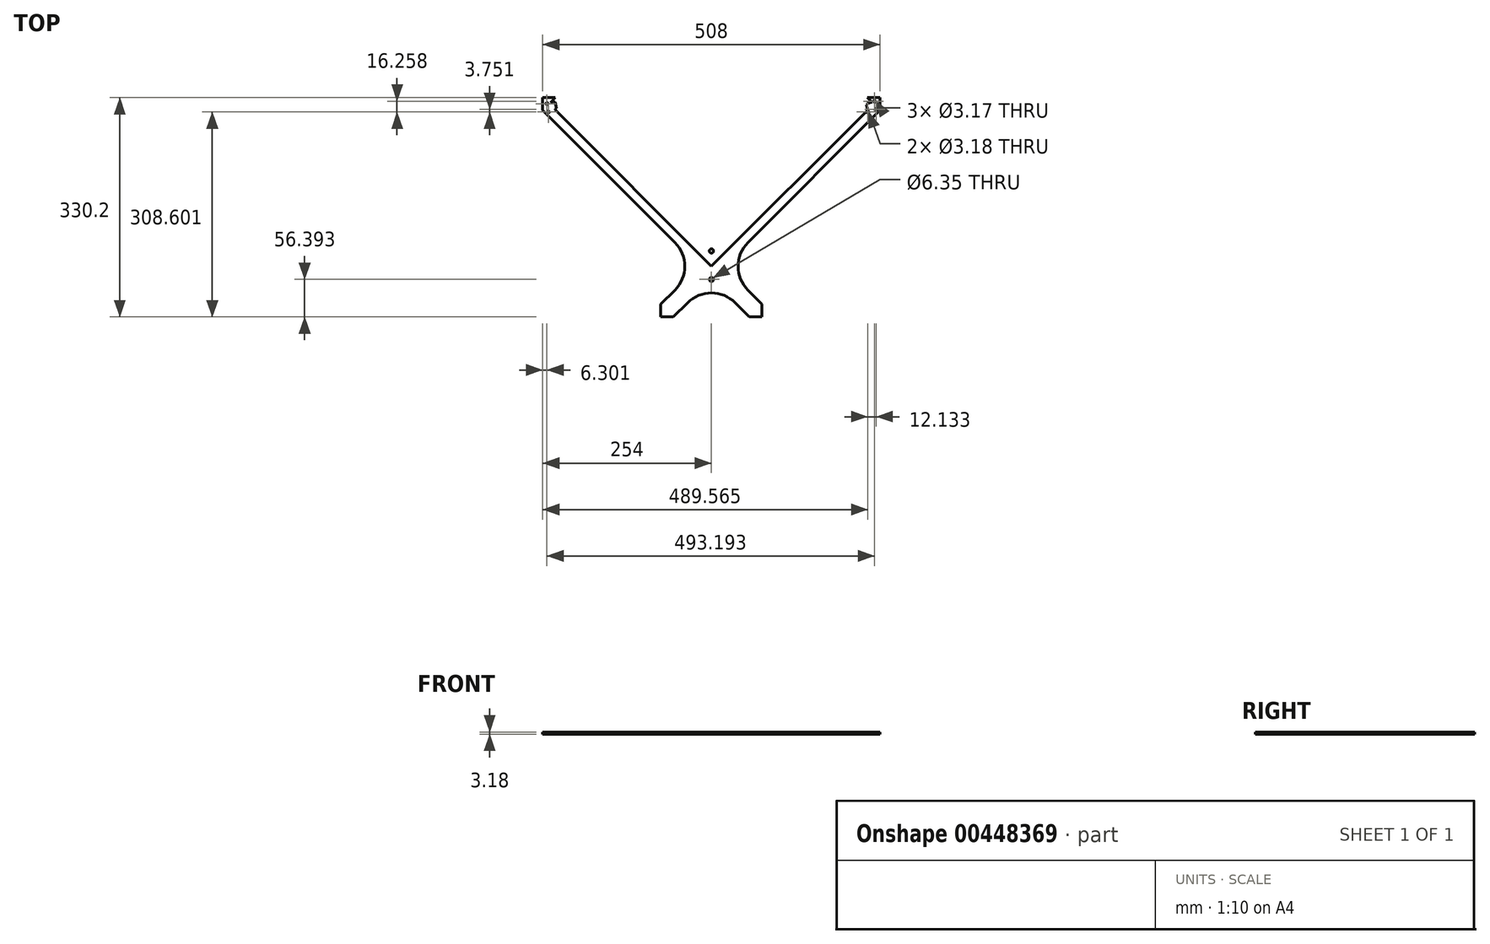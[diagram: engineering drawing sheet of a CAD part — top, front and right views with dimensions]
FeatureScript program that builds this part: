
annotation { "Feature Type Name" : "Feature", "Feature Type Description" : "" }
export const myFeature = defineFeature(function(context is Context, id is Id, definition is map)
    precondition{}
    {
        {
            var Q0;
            Q0=qCreatedBy(makeId("Top.planeOp"),FACE);
            var sketch = newSketch(context, id + "F0", { "sketchPlane" : qUnion([Q0])});
            skLineSegment(sketch, "E0.bottom", {"start": v(254, 254) * mm, "end": v(-254, 254) * mm});
            skLineSegment(sketch, "E0.top", {"start": v(254, -254) * mm, "end": v(-254, -254) * mm});
            skLineSegment(sketch, "E0.left", {"start": v(254, 254) * mm, "end": v(254, -254) * mm});
            skLineSegment(sketch, "E0.right", {"start": v(-254, 254) * mm, "end": v(-254, -254) * mm});
            skPoint(sketch, "E0.middle", {"position": v(0, 0) * mm});
            skSolve(sketch);
        }
        {
            var Q0;
            Q0=makeQuery(id+"F0.imprint","IMPRINT",FACE,{"disambiguationData":[TD([[makeQuery(id+"F0.imprint","IMPRINT",EDGE,{"derivedFrom":sQuery(id+"F0.wireOp",EDGE,"E0.bottom")}),1.0]])]});
            extrude(context, id + "F1", {"entities" : qUnion([Q0]), "depth" : 3.17 * mm});
        }
        {
            var Q0;
            Q0=makeQuery(id+"F1.opExtrude","CAP_FACE",FACE,{"disambiguationData":[OSD([sQuery(id+"F0.wireOp",EDGE,"E0.bottom"),sQuery(id+"F0.wireOp",EDGE,"E0.top"),sQuery(id+"F0.wireOp",EDGE,"E0.left"),sQuery(id+"F0.wireOp",EDGE,"E0.right")])],"isStart":false});
            var sketch = newSketch(context, id + "F2", { "sketchPlane" : qUnion([Q0])});
            skLineSegment(sketch, "E1", {"start": v(0, 19.05) * mm, "end": v(234.95, 254) * mm});
            skLineSegment(sketch, "E2", {"start": v(19.05, 0) * mm, "end": v(254, 234.95) * mm});
            skLineSegment(sketch, "E3.MirrorCS", {"start": v(0, 19.05) * mm, "end": v(-234.95, 254) * mm});
            skLineSegment(sketch, "E4.MirrorCS", {"start": v(-19.05, 0) * mm, "end": v(-254, 234.95) * mm});
            skLineSegment(sketch, "E5.MirrorCS", {"start": v(19.05, 0) * mm, "end": v(254, -234.95) * mm});
            skLineSegment(sketch, "E6.MirrorCS", {"start": v(-19.05, 0) * mm, "end": v(-254, -234.95) * mm});
            skLineSegment(sketch, "E7.MirrorCS", {"start": v(0, -19.05) * mm, "end": v(-234.95, -254) * mm});
            skLineSegment(sketch, "E8.MirrorCS", {"start": v(0, -19.05) * mm, "end": v(234.95, -254) * mm});
            skLineSegment(sketch, "E9", {"start": v(-234.95, 254) * mm, "end": v(234.95, 254) * mm});
            skLineSegment(sketch, "E10", {"start": v(254, 234.95) * mm, "end": v(254, -234.95) * mm});
            skLineSegment(sketch, "E11", {"start": v(-254, -234.95) * mm, "end": v(-254, 234.95) * mm});
            skLineSegment(sketch, "E12", {"start": v(-234.95, -254) * mm, "end": v(234.95, -254) * mm});
            skLineSegment(sketch, "E13", {"start": v(0, 0) * mm, "end": v(254, -254) * mm});
            skSolve(sketch);
        }
        {
            var Q0;
            Q0=makeQuery(id+"F2.imprint","IMPRINT",FACE,{"disambiguationData":[TD([[makeQuery(id+"F2.imprint","IMPRINT",EDGE,{"derivedFrom":sQuery(id+"F2.wireOp",EDGE,"E4.MirrorCS")}),1.0]])]});
            var Q1;
            Q1=makeQuery(id+"F2.imprint","IMPRINT",FACE,{"disambiguationData":[TD([[makeQuery(id+"F2.imprint","IMPRINT",EDGE,{"derivedFrom":sQuery(id+"F2.wireOp",EDGE,"E1")}),1.0]])]});
            var Q2;
            Q2=makeQuery(id+"F2.imprint","IMPRINT",FACE,{"disambiguationData":[TD([[makeQuery(id+"F2.imprint","IMPRINT",EDGE,{"derivedFrom":sQuery(id+"F2.wireOp",EDGE,"E2")}),-1.0]])]});
            var Q3;
            Q3=makeQuery(id+"F2.imprint","IMPRINT",FACE,{"disambiguationData":[TD([[makeQuery(id+"F2.imprint","IMPRINT",EDGE,{"derivedFrom":sQuery(id+"F2.wireOp",EDGE,"E7.MirrorCS")}),1.0]])]});
            extrude(context, id + "F3", {"entities" : qUnion([Q0, Q1, Q2, Q3]), "operationType" : NewBodyOperationType.REMOVE, "endBound" : BoundingType.THROUGH_ALL, "oppositeDirection" : true, "depth" : 25.4 * mm});
        }
        {
            var Q0;
            Q0=makeQuery(id+"F3.boolean.opBoolean","COPY",EDGE,{"derivedFrom":makeQuery(id+"F3.opExtrude","SWEPT_EDGE",EDGE,{"disambiguationData":[OSD([sQuery(id+"F2.wireOp",EDGE,"E4.MirrorCS"),sQuery(id+"F2.wireOp",EDGE,"E6.MirrorCS")])]})});
            var Q1;
            Q1=makeQuery(id+"F3.boolean.opBoolean","COPY",EDGE,{"derivedFrom":makeQuery(id+"F3.opExtrude","SWEPT_EDGE",EDGE,{"disambiguationData":[OSD([sQuery(id+"F2.wireOp",EDGE,"E7.MirrorCS"),sQuery(id+"F2.wireOp",EDGE,"E8.MirrorCS")])]})});
            var Q2;
            Q2=makeQuery(id+"F3.boolean.opBoolean","COPY",EDGE,{"derivedFrom":makeQuery(id+"F3.opExtrude","SWEPT_EDGE",EDGE,{"disambiguationData":[OSD([sQuery(id+"F2.wireOp",EDGE,"E2"),sQuery(id+"F2.wireOp",EDGE,"E5.MirrorCS")])]})});
            var Q3;
            Q3=makeQuery(id+"F3.boolean.opBoolean","COPY",EDGE,{"derivedFrom":makeQuery(id+"F3.opExtrude","SWEPT_EDGE",EDGE,{"disambiguationData":[OSD([sQuery(id+"F2.wireOp",EDGE,"E1"),sQuery(id+"F2.wireOp",EDGE,"E3.MirrorCS")])]})});
            fillet(context, id + "F4", {"entities" : qUnion([Q0, Q1, Q2, Q3]), "radius" : 50.8 * mm, "tangentPropagation" : true, "allowEdgeOverflow" : false});
        }
        {
            var Q0;
            Q0=makeQuery(id+"F1.opExtrude","CAP_FACE",FACE,{"disambiguationData":[OSD([sQuery(id+"F0.wireOp",EDGE,"E0.bottom"),sQuery(id+"F0.wireOp",EDGE,"E0.top"),sQuery(id+"F0.wireOp",EDGE,"E0.left"),sQuery(id+"F0.wireOp",EDGE,"E0.right")])],"isStart":true});
            var sketch = newSketch(context, id + "F5", { "sketchPlane" : qUnion([Q0])});
            skLineSegment(sketch, "E14", {"start": v(-40.1, 0) * mm, "end": v(40.1, 0) * mm});
            skLineSegment(sketch, "E15", {"start": v(0, 40.1) * mm, "end": v(0, -40.1) * mm});
            skLineSegment(sketch, "E16", {"start": v(0, 0) * mm, "end": v(-254, -254) * mm});
            skLineSegment(sketch, "E17", {"start": v(0, 0) * mm, "end": v(254, -254) * mm});
            skLineSegment(sketch, "E18", {"start": v(0, 0) * mm, "end": v(254, 254) * mm});
            skLineSegment(sketch, "E19", {"start": v(234.95, -254) * mm, "end": v(254, -234.95) * mm});
            skLineSegment(sketch, "E20", {"start": v(-254, -234.95) * mm, "end": v(-234.95, -254) * mm});
            skLineSegment(sketch, "E21", {"start": v(234.95, 254) * mm, "end": v(254, 234.95) * mm});
            skLineSegment(sketch, "E22", {"start": v(-254, 234.95) * mm, "end": v(-234.95, 254) * mm});
            skCircle(sketch, "E23", {"center": v(247.7, -236.15) * mm, "radius": 1.59 * mm});
            skCircle(sketch, "E24", {"center": v(-125.31, -108.96) * mm, "radius": 1.59 * mm});
            skCircle(sketch, "E25", {"center": v(235.57, -232.4) * mm, "radius": 1.59 * mm});
            skCircle(sketch, "E26", {"center": v(245.5, -248.66) * mm, "radius": 1.59 * mm});
            skCircle(sketch, "E27", {"center": v(233.36, -244.9) * mm, "radius": 1.59 * mm});
            skLineSegment(sketch, "E28", {"start": v(247.7, -236.15) * mm, "end": v(235.57, -232.4) * mm});
            skLineSegment(sketch, "E29", {"start": v(247.7, -236.15) * mm, "end": v(245.5, -248.66) * mm});
            skLineSegment(sketch, "E30", {"start": v(235.57, -232.4) * mm, "end": v(233.36, -244.9) * mm});
            skLineSegment(sketch, "E31", {"start": v(233.36, -244.9) * mm, "end": v(245.5, -248.66) * mm});
            skLineSegment(sketch, "E32", {"start": v(245.5, -248.66) * mm, "end": v(235.57, -232.4) * mm});
            skPoint(sketch, "E33.endSnap0", {"position": v(240.53, -240.53) * mm});
            skCircle(sketch, "E34", {"center": v(-233.36, -236.15) * mm, "radius": 1.59 * mm});
            skCircle(sketch, "E35", {"center": v(-245.5, -232.4) * mm, "radius": 1.59 * mm});
            skCircle(sketch, "E36", {"center": v(-235.57, -248.66) * mm, "radius": 1.59 * mm});
            skCircle(sketch, "E37", {"center": v(-247.7, -244.9) * mm, "radius": 1.59 * mm});
            skLineSegment(sketch, "E38", {"start": v(-233.36, -236.15) * mm, "end": v(-245.5, -232.4) * mm});
            skLineSegment(sketch, "E39", {"start": v(-233.36, -236.15) * mm, "end": v(-235.57, -248.66) * mm});
            skLineSegment(sketch, "E40", {"start": v(-245.5, -232.4) * mm, "end": v(-247.7, -244.9) * mm});
            skLineSegment(sketch, "E41", {"start": v(-247.7, -244.9) * mm, "end": v(-235.57, -248.66) * mm});
            skLineSegment(sketch, "E42", {"start": v(-235.57, -248.66) * mm, "end": v(-245.5, -232.4) * mm});
            skPoint(sketch, "E43.endSnap0", {"position": v(-240.53, -240.53) * mm});
            skCircle(sketch, "E44", {"center": v(247.7, 244.9) * mm, "radius": 1.59 * mm});
            skCircle(sketch, "E45", {"center": v(235.57, 248.66) * mm, "radius": 1.59 * mm});
            skCircle(sketch, "E46", {"center": v(245.5, 232.4) * mm, "radius": 1.59 * mm});
            skCircle(sketch, "E47", {"center": v(233.36, 236.15) * mm, "radius": 1.59 * mm});
            skLineSegment(sketch, "E48", {"start": v(247.7, 244.9) * mm, "end": v(235.57, 248.66) * mm});
            skLineSegment(sketch, "E49", {"start": v(247.7, 244.9) * mm, "end": v(245.5, 232.4) * mm});
            skLineSegment(sketch, "E50", {"start": v(235.57, 248.66) * mm, "end": v(233.36, 236.15) * mm});
            skLineSegment(sketch, "E51", {"start": v(233.36, 236.15) * mm, "end": v(245.5, 232.4) * mm});
            skLineSegment(sketch, "E52", {"start": v(245.5, 232.4) * mm, "end": v(235.57, 248.66) * mm});
            skPoint(sketch, "E53.endSnap0", {"position": v(240.53, 240.53) * mm});
            skCircle(sketch, "E54", {"center": v(-233.36, 244.9) * mm, "radius": 1.59 * mm});
            skCircle(sketch, "E55", {"center": v(-245.5, 248.66) * mm, "radius": 1.59 * mm});
            skCircle(sketch, "E56", {"center": v(-235.57, 232.4) * mm, "radius": 1.59 * mm});
            skCircle(sketch, "E57", {"center": v(-247.7, 236.15) * mm, "radius": 1.59 * mm});
            skLineSegment(sketch, "E58", {"start": v(-233.36, 244.9) * mm, "end": v(-245.5, 248.66) * mm});
            skLineSegment(sketch, "E59", {"start": v(-233.36, 244.9) * mm, "end": v(-235.57, 232.4) * mm});
            skLineSegment(sketch, "E60", {"start": v(-245.5, 248.66) * mm, "end": v(-247.7, 236.15) * mm});
            skLineSegment(sketch, "E61", {"start": v(-247.7, 236.15) * mm, "end": v(-235.57, 232.4) * mm});
            skLineSegment(sketch, "E62", {"start": v(-235.57, 232.4) * mm, "end": v(-245.5, 248.66) * mm});
            skPoint(sketch, "E63.endSnap0", {"position": v(-240.53, 240.53) * mm});
            skLineSegment(sketch, "E64", {"start": v(-254, 254) * mm, "end": v(0, 0) * mm});
            skCircle(sketch, "E65", {"center": v(0, -23.16) * mm, "radius": 3.18 * mm});
            skCircle(sketch, "E66", {"center": v(0, 19.8) * mm, "radius": 3.18 * mm});
            skSolve(sketch);
        }
        {
            var Q0;
            {var subQ0=sQuery(id+"F5.wireOp",EDGE,"E42");var subQ1=sQuery(id+"F5.wireOp",EDGE,"E36");var subQ2=makeQuery(id+"F5.imprint","INTERSECT",VERTEX,{"derivedFrom":[subQ1,subQ0]});Q0=makeQuery(id+"F5.imprint","IMPRINT",FACE,{"disambiguationData":[TD([[makeQuery(id+"F5.imprint","IMPRINT",EDGE,{"disambiguationData":[TD([[subQ2,1.0]])],"derivedFrom":subQ1}),1.0]])]});}
            var Q1;
            {var subQ0=sQuery(id+"F5.wireOp",EDGE,"E42");var subQ1=sQuery(id+"F5.wireOp",EDGE,"E36");var subQ2=makeQuery(id+"F5.imprint","INTERSECT",VERTEX,{"derivedFrom":[subQ1,subQ0]});Q1=makeQuery(id+"F5.imprint","IMPRINT",FACE,{"disambiguationData":[TD([[makeQuery(id+"F5.imprint","IMPRINT",EDGE,{"disambiguationData":[TD([[subQ2,-1.0]])],"derivedFrom":subQ1}),1.0]])]});}
            var Q2;
            {var subQ0=sQuery(id+"F5.wireOp",EDGE,"E39");var subQ1=sQuery(id+"F5.wireOp",EDGE,"E36");var subQ2=makeQuery(id+"F5.imprint","INTERSECT",VERTEX,{"derivedFrom":[subQ1,subQ0]});Q2=makeQuery(id+"F5.imprint","IMPRINT",FACE,{"disambiguationData":[TD([[makeQuery(id+"F5.imprint","IMPRINT",EDGE,{"disambiguationData":[TD([[subQ2,1.0]])],"derivedFrom":subQ1}),1.0]])]});}
            var Q3;
            {var subQ0=sQuery(id+"F5.wireOp",EDGE,"E40");var subQ1=sQuery(id+"F5.wireOp",EDGE,"E37");var subQ2=makeQuery(id+"F5.imprint","INTERSECT",VERTEX,{"derivedFrom":[subQ1,subQ0]});Q3=makeQuery(id+"F5.imprint","IMPRINT",FACE,{"disambiguationData":[TD([[makeQuery(id+"F5.imprint","IMPRINT",EDGE,{"disambiguationData":[TD([[subQ2,-1.0]])],"derivedFrom":subQ1}),1.0]])]});}
            var Q4;
            {var subQ0=sQuery(id+"F5.wireOp",EDGE,"E42");var subQ1=sQuery(id+"F5.wireOp",EDGE,"E35");var subQ2=makeQuery(id+"F5.imprint","INTERSECT",VERTEX,{"derivedFrom":[subQ1,subQ0]});Q4=makeQuery(id+"F5.imprint","IMPRINT",FACE,{"disambiguationData":[TD([[makeQuery(id+"F5.imprint","IMPRINT",EDGE,{"disambiguationData":[TD([[subQ2,-1.0]])],"derivedFrom":subQ1}),1.0]])]});}
            var Q5;
            {var subQ0=sQuery(id+"F5.wireOp",EDGE,"E42");var subQ1=sQuery(id+"F5.wireOp",EDGE,"E35");var subQ2=makeQuery(id+"F5.imprint","INTERSECT",VERTEX,{"derivedFrom":[subQ1,subQ0]});Q5=makeQuery(id+"F5.imprint","IMPRINT",FACE,{"disambiguationData":[TD([[makeQuery(id+"F5.imprint","IMPRINT",EDGE,{"disambiguationData":[TD([[subQ2,1.0]])],"derivedFrom":subQ1}),1.0]])]});}
            var Q6;
            {var subQ0=sQuery(id+"F5.wireOp",EDGE,"E40");var subQ1=sQuery(id+"F5.wireOp",EDGE,"E35");var subQ2=makeQuery(id+"F5.imprint","INTERSECT",VERTEX,{"derivedFrom":[subQ1,subQ0]});Q6=makeQuery(id+"F5.imprint","IMPRINT",FACE,{"disambiguationData":[TD([[makeQuery(id+"F5.imprint","IMPRINT",EDGE,{"disambiguationData":[TD([[subQ2,1.0]])],"derivedFrom":subQ1}),1.0]])]});}
            var Q7;
            {var subQ0=sQuery(id+"F5.wireOp",EDGE,"E38");var subQ1=sQuery(id+"F5.wireOp",EDGE,"E34");var subQ2=makeQuery(id+"F5.imprint","INTERSECT",VERTEX,{"derivedFrom":[subQ1,subQ0]});Q7=makeQuery(id+"F5.imprint","IMPRINT",FACE,{"disambiguationData":[TD([[makeQuery(id+"F5.imprint","IMPRINT",EDGE,{"disambiguationData":[TD([[subQ2,1.0]])],"derivedFrom":subQ1}),1.0]])]});}
            var Q8;
            {var subQ0=sQuery(id+"F5.wireOp",EDGE,"E38");var subQ1=sQuery(id+"F5.wireOp",EDGE,"E34");var subQ2=makeQuery(id+"F5.imprint","INTERSECT",VERTEX,{"derivedFrom":[subQ1,subQ0]});Q8=makeQuery(id+"F5.imprint","IMPRINT",FACE,{"disambiguationData":[TD([[makeQuery(id+"F5.imprint","IMPRINT",EDGE,{"disambiguationData":[TD([[subQ2,-1.0]])],"derivedFrom":subQ1}),1.0]])]});}
            var Q9;
            {var subQ0=sQuery(id+"F5.wireOp",EDGE,"E40");var subQ1=sQuery(id+"F5.wireOp",EDGE,"E37");var subQ2=makeQuery(id+"F5.imprint","INTERSECT",VERTEX,{"derivedFrom":[subQ1,subQ0]});Q9=makeQuery(id+"F5.imprint","IMPRINT",FACE,{"disambiguationData":[TD([[makeQuery(id+"F5.imprint","IMPRINT",EDGE,{"disambiguationData":[TD([[subQ2,1.0]])],"derivedFrom":subQ1}),1.0]])]});}
            var Q10;
            {var subQ0=sQuery(id+"F5.wireOp",EDGE,"E58");var subQ1=sQuery(id+"F5.wireOp",EDGE,"E54");var subQ2=makeQuery(id+"F5.imprint","INTERSECT",VERTEX,{"derivedFrom":[subQ1,subQ0]});Q10=makeQuery(id+"F5.imprint","IMPRINT",FACE,{"disambiguationData":[TD([[makeQuery(id+"F5.imprint","IMPRINT",EDGE,{"disambiguationData":[TD([[subQ2,1.0]])],"derivedFrom":subQ1}),1.0]])]});}
            var Q11;
            {var subQ0=sQuery(id+"F5.wireOp",EDGE,"E58");var subQ1=sQuery(id+"F5.wireOp",EDGE,"E54");var subQ2=makeQuery(id+"F5.imprint","INTERSECT",VERTEX,{"derivedFrom":[subQ1,subQ0]});Q11=makeQuery(id+"F5.imprint","IMPRINT",FACE,{"disambiguationData":[TD([[makeQuery(id+"F5.imprint","IMPRINT",EDGE,{"disambiguationData":[TD([[subQ2,-1.0]])],"derivedFrom":subQ1}),1.0]])]});}
            var Q12;
            {var subQ0=sQuery(id+"F5.wireOp",EDGE,"E62");var subQ1=sQuery(id+"F5.wireOp",EDGE,"E55");var subQ2=makeQuery(id+"F5.imprint","INTERSECT",VERTEX,{"derivedFrom":[subQ1,subQ0]});Q12=makeQuery(id+"F5.imprint","IMPRINT",FACE,{"disambiguationData":[TD([[makeQuery(id+"F5.imprint","IMPRINT",EDGE,{"disambiguationData":[TD([[subQ2,-1.0]])],"derivedFrom":subQ1}),1.0]])]});}
            var Q13;
            {var subQ0=sQuery(id+"F5.wireOp",EDGE,"E62");var subQ1=sQuery(id+"F5.wireOp",EDGE,"E55");var subQ2=makeQuery(id+"F5.imprint","INTERSECT",VERTEX,{"derivedFrom":[subQ1,subQ0]});Q13=makeQuery(id+"F5.imprint","IMPRINT",FACE,{"disambiguationData":[TD([[makeQuery(id+"F5.imprint","IMPRINT",EDGE,{"disambiguationData":[TD([[subQ2,1.0]])],"derivedFrom":subQ1}),1.0]])]});}
            var Q14;
            {var subQ0=sQuery(id+"F5.wireOp",EDGE,"E60");var subQ1=sQuery(id+"F5.wireOp",EDGE,"E55");var subQ2=makeQuery(id+"F5.imprint","INTERSECT",VERTEX,{"derivedFrom":[subQ1,subQ0]});Q14=makeQuery(id+"F5.imprint","IMPRINT",FACE,{"disambiguationData":[TD([[makeQuery(id+"F5.imprint","IMPRINT",EDGE,{"disambiguationData":[TD([[subQ2,1.0]])],"derivedFrom":subQ1}),1.0]])]});}
            var Q15;
            {var subQ0=sQuery(id+"F5.wireOp",EDGE,"E60");var subQ1=sQuery(id+"F5.wireOp",EDGE,"E57");var subQ2=makeQuery(id+"F5.imprint","INTERSECT",VERTEX,{"derivedFrom":[subQ1,subQ0]});Q15=makeQuery(id+"F5.imprint","IMPRINT",FACE,{"disambiguationData":[TD([[makeQuery(id+"F5.imprint","IMPRINT",EDGE,{"disambiguationData":[TD([[subQ2,1.0]])],"derivedFrom":subQ1}),1.0]])]});}
            var Q16;
            {var subQ0=sQuery(id+"F5.wireOp",EDGE,"E60");var subQ1=sQuery(id+"F5.wireOp",EDGE,"E57");var subQ2=makeQuery(id+"F5.imprint","INTERSECT",VERTEX,{"derivedFrom":[subQ1,subQ0]});Q16=makeQuery(id+"F5.imprint","IMPRINT",FACE,{"disambiguationData":[TD([[makeQuery(id+"F5.imprint","IMPRINT",EDGE,{"disambiguationData":[TD([[subQ2,-1.0]])],"derivedFrom":subQ1}),1.0]])]});}
            var Q17;
            {var subQ0=sQuery(id+"F5.wireOp",EDGE,"E59");var subQ1=sQuery(id+"F5.wireOp",EDGE,"E56");var subQ2=makeQuery(id+"F5.imprint","INTERSECT",VERTEX,{"derivedFrom":[subQ1,subQ0]});Q17=makeQuery(id+"F5.imprint","IMPRINT",FACE,{"disambiguationData":[TD([[makeQuery(id+"F5.imprint","IMPRINT",EDGE,{"disambiguationData":[TD([[subQ2,1.0]])],"derivedFrom":subQ1}),1.0]])]});}
            var Q18;
            {var subQ0=sQuery(id+"F5.wireOp",EDGE,"E62");var subQ1=sQuery(id+"F5.wireOp",EDGE,"E56");var subQ2=makeQuery(id+"F5.imprint","INTERSECT",VERTEX,{"derivedFrom":[subQ1,subQ0]});Q18=makeQuery(id+"F5.imprint","IMPRINT",FACE,{"disambiguationData":[TD([[makeQuery(id+"F5.imprint","IMPRINT",EDGE,{"disambiguationData":[TD([[subQ2,1.0]])],"derivedFrom":subQ1}),1.0]])]});}
            var Q19;
            {var subQ0=sQuery(id+"F5.wireOp",EDGE,"E62");var subQ1=sQuery(id+"F5.wireOp",EDGE,"E56");var subQ2=makeQuery(id+"F5.imprint","INTERSECT",VERTEX,{"derivedFrom":[subQ1,subQ0]});Q19=makeQuery(id+"F5.imprint","IMPRINT",FACE,{"disambiguationData":[TD([[makeQuery(id+"F5.imprint","IMPRINT",EDGE,{"disambiguationData":[TD([[subQ2,-1.0]])],"derivedFrom":subQ1}),1.0]])]});}
            var Q20;
            {var subQ0=sQuery(id+"F5.wireOp",EDGE,"E48");var subQ1=sQuery(id+"F5.wireOp",EDGE,"E44");var subQ2=makeQuery(id+"F5.imprint","INTERSECT",VERTEX,{"derivedFrom":[subQ1,subQ0]});Q20=makeQuery(id+"F5.imprint","IMPRINT",FACE,{"disambiguationData":[TD([[makeQuery(id+"F5.imprint","IMPRINT",EDGE,{"disambiguationData":[TD([[subQ2,1.0]])],"derivedFrom":subQ1}),1.0]])]});}
            var Q21;
            {var subQ0=sQuery(id+"F5.wireOp",EDGE,"E48");var subQ1=sQuery(id+"F5.wireOp",EDGE,"E44");var subQ2=makeQuery(id+"F5.imprint","INTERSECT",VERTEX,{"derivedFrom":[subQ1,subQ0]});Q21=makeQuery(id+"F5.imprint","IMPRINT",FACE,{"disambiguationData":[TD([[makeQuery(id+"F5.imprint","IMPRINT",EDGE,{"disambiguationData":[TD([[subQ2,-1.0]])],"derivedFrom":subQ1}),1.0]])]});}
            var Q22;
            {var subQ0=sQuery(id+"F5.wireOp",EDGE,"E52");var subQ1=sQuery(id+"F5.wireOp",EDGE,"E46");var subQ2=makeQuery(id+"F5.imprint","INTERSECT",VERTEX,{"derivedFrom":[subQ1,subQ0]});Q22=makeQuery(id+"F5.imprint","IMPRINT",FACE,{"disambiguationData":[TD([[makeQuery(id+"F5.imprint","IMPRINT",EDGE,{"disambiguationData":[TD([[subQ2,1.0]])],"derivedFrom":subQ1}),1.0]])]});}
            var Q23;
            {var subQ0=sQuery(id+"F5.wireOp",EDGE,"E49");var subQ1=sQuery(id+"F5.wireOp",EDGE,"E46");var subQ2=makeQuery(id+"F5.imprint","INTERSECT",VERTEX,{"derivedFrom":[subQ1,subQ0]});Q23=makeQuery(id+"F5.imprint","IMPRINT",FACE,{"disambiguationData":[TD([[makeQuery(id+"F5.imprint","IMPRINT",EDGE,{"disambiguationData":[TD([[subQ2,1.0]])],"derivedFrom":subQ1}),1.0]])]});}
            var Q24;
            {var subQ0=sQuery(id+"F5.wireOp",EDGE,"E52");var subQ1=sQuery(id+"F5.wireOp",EDGE,"E46");var subQ2=makeQuery(id+"F5.imprint","INTERSECT",VERTEX,{"derivedFrom":[subQ1,subQ0]});Q24=makeQuery(id+"F5.imprint","IMPRINT",FACE,{"disambiguationData":[TD([[makeQuery(id+"F5.imprint","IMPRINT",EDGE,{"disambiguationData":[TD([[subQ2,-1.0]])],"derivedFrom":subQ1}),1.0]])]});}
            var Q25;
            {var subQ0=sQuery(id+"F5.wireOp",EDGE,"E50");var subQ1=sQuery(id+"F5.wireOp",EDGE,"E47");var subQ2=makeQuery(id+"F5.imprint","INTERSECT",VERTEX,{"derivedFrom":[subQ1,subQ0]});Q25=makeQuery(id+"F5.imprint","IMPRINT",FACE,{"disambiguationData":[TD([[makeQuery(id+"F5.imprint","IMPRINT",EDGE,{"disambiguationData":[TD([[subQ2,-1.0]])],"derivedFrom":subQ1}),1.0]])]});}
            var Q26;
            {var subQ0=sQuery(id+"F5.wireOp",EDGE,"E50");var subQ1=sQuery(id+"F5.wireOp",EDGE,"E47");var subQ2=makeQuery(id+"F5.imprint","INTERSECT",VERTEX,{"derivedFrom":[subQ1,subQ0]});Q26=makeQuery(id+"F5.imprint","IMPRINT",FACE,{"disambiguationData":[TD([[makeQuery(id+"F5.imprint","IMPRINT",EDGE,{"disambiguationData":[TD([[subQ2,1.0]])],"derivedFrom":subQ1}),1.0]])]});}
            var Q27;
            {var subQ0=sQuery(id+"F5.wireOp",EDGE,"E52");var subQ1=sQuery(id+"F5.wireOp",EDGE,"E45");var subQ2=makeQuery(id+"F5.imprint","INTERSECT",VERTEX,{"derivedFrom":[subQ1,subQ0]});Q27=makeQuery(id+"F5.imprint","IMPRINT",FACE,{"disambiguationData":[TD([[makeQuery(id+"F5.imprint","IMPRINT",EDGE,{"disambiguationData":[TD([[subQ2,1.0]])],"derivedFrom":subQ1}),1.0]])]});}
            var Q28;
            {var subQ0=sQuery(id+"F5.wireOp",EDGE,"E52");var subQ1=sQuery(id+"F5.wireOp",EDGE,"E45");var subQ2=makeQuery(id+"F5.imprint","INTERSECT",VERTEX,{"derivedFrom":[subQ1,subQ0]});Q28=makeQuery(id+"F5.imprint","IMPRINT",FACE,{"disambiguationData":[TD([[makeQuery(id+"F5.imprint","IMPRINT",EDGE,{"disambiguationData":[TD([[subQ2,-1.0]])],"derivedFrom":subQ1}),1.0]])]});}
            var Q29;
            {var subQ0=sQuery(id+"F5.wireOp",EDGE,"E50");var subQ1=sQuery(id+"F5.wireOp",EDGE,"E45");var subQ2=makeQuery(id+"F5.imprint","INTERSECT",VERTEX,{"derivedFrom":[subQ1,subQ0]});Q29=makeQuery(id+"F5.imprint","IMPRINT",FACE,{"disambiguationData":[TD([[makeQuery(id+"F5.imprint","IMPRINT",EDGE,{"disambiguationData":[TD([[subQ2,1.0]])],"derivedFrom":subQ1}),1.0]])]});}
            var Q30;
            {var subQ0=sQuery(id+"F5.wireOp",EDGE,"E29");var subQ1=sQuery(id+"F5.wireOp",EDGE,"E26");var subQ2=makeQuery(id+"F5.imprint","INTERSECT",VERTEX,{"derivedFrom":[subQ1,subQ0]});Q30=makeQuery(id+"F5.imprint","IMPRINT",FACE,{"disambiguationData":[TD([[makeQuery(id+"F5.imprint","IMPRINT",EDGE,{"disambiguationData":[TD([[subQ2,1.0]])],"derivedFrom":subQ1}),1.0]])]});}
            var Q31;
            {var subQ0=sQuery(id+"F5.wireOp",EDGE,"E32");var subQ1=sQuery(id+"F5.wireOp",EDGE,"E26");var subQ2=makeQuery(id+"F5.imprint","INTERSECT",VERTEX,{"derivedFrom":[subQ1,subQ0]});Q31=makeQuery(id+"F5.imprint","IMPRINT",FACE,{"disambiguationData":[TD([[makeQuery(id+"F5.imprint","IMPRINT",EDGE,{"disambiguationData":[TD([[subQ2,-1.0]])],"derivedFrom":subQ1}),1.0]])]});}
            var Q32;
            {var subQ0=sQuery(id+"F5.wireOp",EDGE,"E32");var subQ1=sQuery(id+"F5.wireOp",EDGE,"E26");var subQ2=makeQuery(id+"F5.imprint","INTERSECT",VERTEX,{"derivedFrom":[subQ1,subQ0]});Q32=makeQuery(id+"F5.imprint","IMPRINT",FACE,{"disambiguationData":[TD([[makeQuery(id+"F5.imprint","IMPRINT",EDGE,{"disambiguationData":[TD([[subQ2,1.0]])],"derivedFrom":subQ1}),1.0]])]});}
            var Q33;
            {var subQ0=sQuery(id+"F5.wireOp",EDGE,"E30");var subQ1=sQuery(id+"F5.wireOp",EDGE,"E27");var subQ2=makeQuery(id+"F5.imprint","INTERSECT",VERTEX,{"derivedFrom":[subQ1,subQ0]});Q33=makeQuery(id+"F5.imprint","IMPRINT",FACE,{"disambiguationData":[TD([[makeQuery(id+"F5.imprint","IMPRINT",EDGE,{"disambiguationData":[TD([[subQ2,1.0]])],"derivedFrom":subQ1}),1.0]])]});}
            var Q34;
            {var subQ0=sQuery(id+"F5.wireOp",EDGE,"E30");var subQ1=sQuery(id+"F5.wireOp",EDGE,"E27");var subQ2=makeQuery(id+"F5.imprint","INTERSECT",VERTEX,{"derivedFrom":[subQ1,subQ0]});Q34=makeQuery(id+"F5.imprint","IMPRINT",FACE,{"disambiguationData":[TD([[makeQuery(id+"F5.imprint","IMPRINT",EDGE,{"disambiguationData":[TD([[subQ2,-1.0]])],"derivedFrom":subQ1}),1.0]])]});}
            var Q35;
            {var subQ0=sQuery(id+"F5.wireOp",EDGE,"E32");var subQ1=sQuery(id+"F5.wireOp",EDGE,"E25");var subQ2=makeQuery(id+"F5.imprint","INTERSECT",VERTEX,{"derivedFrom":[subQ1,subQ0]});Q35=makeQuery(id+"F5.imprint","IMPRINT",FACE,{"disambiguationData":[TD([[makeQuery(id+"F5.imprint","IMPRINT",EDGE,{"disambiguationData":[TD([[subQ2,1.0]])],"derivedFrom":subQ1}),1.0]])]});}
            var Q36;
            {var subQ0=sQuery(id+"F5.wireOp",EDGE,"E32");var subQ1=sQuery(id+"F5.wireOp",EDGE,"E25");var subQ2=makeQuery(id+"F5.imprint","INTERSECT",VERTEX,{"derivedFrom":[subQ1,subQ0]});Q36=makeQuery(id+"F5.imprint","IMPRINT",FACE,{"disambiguationData":[TD([[makeQuery(id+"F5.imprint","IMPRINT",EDGE,{"disambiguationData":[TD([[subQ2,-1.0]])],"derivedFrom":subQ1}),1.0]])]});}
            var Q37;
            {var subQ0=sQuery(id+"F5.wireOp",EDGE,"E30");var subQ1=sQuery(id+"F5.wireOp",EDGE,"E25");var subQ2=makeQuery(id+"F5.imprint","INTERSECT",VERTEX,{"derivedFrom":[subQ1,subQ0]});Q37=makeQuery(id+"F5.imprint","IMPRINT",FACE,{"disambiguationData":[TD([[makeQuery(id+"F5.imprint","IMPRINT",EDGE,{"disambiguationData":[TD([[subQ2,1.0]])],"derivedFrom":subQ1}),1.0]])]});}
            var Q38;
            {var subQ0=sQuery(id+"F5.wireOp",EDGE,"E28");var subQ1=sQuery(id+"F5.wireOp",EDGE,"E23");var subQ2=makeQuery(id+"F5.imprint","INTERSECT",VERTEX,{"derivedFrom":[subQ1,subQ0]});Q38=makeQuery(id+"F5.imprint","IMPRINT",FACE,{"disambiguationData":[TD([[makeQuery(id+"F5.imprint","IMPRINT",EDGE,{"disambiguationData":[TD([[subQ2,-1.0]])],"derivedFrom":subQ1}),1.0]])]});}
            var Q39;
            {var subQ0=sQuery(id+"F5.wireOp",EDGE,"E28");var subQ1=sQuery(id+"F5.wireOp",EDGE,"E23");var subQ2=makeQuery(id+"F5.imprint","INTERSECT",VERTEX,{"derivedFrom":[subQ1,subQ0]});Q39=makeQuery(id+"F5.imprint","IMPRINT",FACE,{"disambiguationData":[TD([[makeQuery(id+"F5.imprint","IMPRINT",EDGE,{"disambiguationData":[TD([[subQ2,1.0]])],"derivedFrom":subQ1}),1.0]])]});}
            var Q40;
            {var subQ0=sQuery(id+"F5.wireOp",EDGE,"E66");var subQ1=sQuery(id+"F5.wireOp",EDGE,"E15");var subQ2=makeQuery(id+"F5.imprint","INTERSECT",VERTEX,{"disambiguationData":[OD(0.0)],"derivedFrom":[subQ1,subQ0]});Q40=makeQuery(id+"F5.imprint","IMPRINT",FACE,{"disambiguationData":[TD([[makeQuery(id+"F5.imprint","IMPRINT",EDGE,{"disambiguationData":[TD([[subQ2,-1.0]])],"derivedFrom":subQ1}),1.0]])]});}
            var Q41;
            {var subQ0=sQuery(id+"F5.wireOp",EDGE,"E65");var subQ1=sQuery(id+"F5.wireOp",EDGE,"E15");var subQ2=makeQuery(id+"F5.imprint","INTERSECT",VERTEX,{"disambiguationData":[OD(0.0)],"derivedFrom":[subQ1,subQ0]});Q41=makeQuery(id+"F5.imprint","IMPRINT",FACE,{"disambiguationData":[TD([[makeQuery(id+"F5.imprint","IMPRINT",EDGE,{"disambiguationData":[TD([[subQ2,-1.0]])],"derivedFrom":subQ1}),-1.0]])]});}
            var Q42;
            {var subQ0=sQuery(id+"F5.wireOp",EDGE,"E65");var subQ1=sQuery(id+"F5.wireOp",EDGE,"E15");var subQ2=makeQuery(id+"F5.imprint","INTERSECT",VERTEX,{"disambiguationData":[OD(0.0)],"derivedFrom":[subQ1,subQ0]});Q42=makeQuery(id+"F5.imprint","IMPRINT",FACE,{"disambiguationData":[TD([[makeQuery(id+"F5.imprint","IMPRINT",EDGE,{"disambiguationData":[TD([[subQ2,-1.0]])],"derivedFrom":subQ1}),1.0]])]});}
            var Q43;
            {var subQ0=sQuery(id+"F5.wireOp",EDGE,"E66");var subQ1=sQuery(id+"F5.wireOp",EDGE,"E15");var subQ2=makeQuery(id+"F5.imprint","INTERSECT",VERTEX,{"disambiguationData":[OD(0.0)],"derivedFrom":[subQ1,subQ0]});Q43=makeQuery(id+"F5.imprint","IMPRINT",FACE,{"disambiguationData":[TD([[makeQuery(id+"F5.imprint","IMPRINT",EDGE,{"disambiguationData":[TD([[subQ2,-1.0]])],"derivedFrom":subQ1}),-1.0]])]});}
            extrude(context, id + "F6", {"entities" : qUnion([Q0, Q1, Q2, Q3, Q4, Q5, Q6, Q7, Q8, Q9, Q10, Q11, Q12, Q13, Q14, Q15, Q16, Q17, Q18, Q19, Q20, Q21, Q22, Q23, Q24, Q25, Q26, Q27, Q28, Q29, Q30, Q31, Q32, Q33, Q34, Q35, Q36, Q37, Q38, Q39, Q40, Q41, Q42, Q43]), "operationType" : NewBodyOperationType.REMOVE, "endBound" : BoundingType.THROUGH_ALL, "oppositeDirection" : true, "depth" : 25.4 * mm});
        }
        {
            var Q0;
            Q0=makeQuery(id+"F1.opExtrude","CAP_FACE",FACE,{"disambiguationData":[OSD([sQuery(id+"F0.wireOp",EDGE,"E0.bottom"),sQuery(id+"F0.wireOp",EDGE,"E0.top"),sQuery(id+"F0.wireOp",EDGE,"E0.left"),sQuery(id+"F0.wireOp",EDGE,"E0.right")])],"isStart":false});
            var sketch = newSketch(context, id + "F7", { "sketchPlane" : qUnion([Q0])});
            skLineSegment(sketch, "E67.bottom", {"start": v(76.2, 76.2) * mm, "end": v(-76.2, 76.2) * mm});
            skLineSegment(sketch, "E67.top", {"start": v(76.2, -76.2) * mm, "end": v(-76.2, -76.2) * mm});
            skLineSegment(sketch, "E67.left", {"start": v(76.2, 76.2) * mm, "end": v(76.2, -76.2) * mm});
            skLineSegment(sketch, "E67.right", {"start": v(-76.2, 76.2) * mm, "end": v(-76.2, -76.2) * mm});
            skPoint(sketch, "E67.middle", {"position": v(0, 0) * mm});
            skLineSegment(sketch, "E68", {"start": v(57.15, 76.2) * mm, "end": v(234.95, 254) * mm});
            skLineSegment(sketch, "E69", {"start": v(234.95, 254) * mm, "end": v(254, 254) * mm});
            skLineSegment(sketch, "E70", {"start": v(254, 254) * mm, "end": v(254, 234.95) * mm});
            skLineSegment(sketch, "E71", {"start": v(254, 234.95) * mm, "end": v(76.2, 57.15) * mm});
            skLineSegment(sketch, "E72.MirrorCS", {"start": v(57.15, -76.2) * mm, "end": v(234.95, -254) * mm});
            skLineSegment(sketch, "E73.MirrorCS", {"start": v(254, -234.95) * mm, "end": v(76.2, -57.15) * mm});
            skLineSegment(sketch, "E74.MirrorCS", {"start": v(234.95, -254) * mm, "end": v(254, -254) * mm});
            skLineSegment(sketch, "E75.MirrorCS", {"start": v(254, -254) * mm, "end": v(254, -234.95) * mm});
            skLineSegment(sketch, "E76.MirrorCS", {"start": v(-57.15, 76.2) * mm, "end": v(-234.95, 254) * mm});
            skLineSegment(sketch, "E77.MirrorCS", {"start": v(-254, 234.95) * mm, "end": v(-76.2, 57.15) * mm});
            skLineSegment(sketch, "E78.MirrorCS", {"start": v(-254, -234.95) * mm, "end": v(-76.2, -57.15) * mm});
            skLineSegment(sketch, "E79.MirrorCS", {"start": v(-57.15, -76.2) * mm, "end": v(-234.95, -254) * mm});
            skLineSegment(sketch, "E80.MirrorCS", {"start": v(-234.95, -254) * mm, "end": v(-254, -254) * mm});
            skLineSegment(sketch, "E81.MirrorCS", {"start": v(-254, -254) * mm, "end": v(-254, -234.95) * mm});
            skLineSegment(sketch, "E82.MirrorCS", {"start": v(-234.95, 254) * mm, "end": v(-254, 254) * mm});
            skLineSegment(sketch, "E83.MirrorCS", {"start": v(-254, 254) * mm, "end": v(-254, 234.95) * mm});
            skSolve(sketch);
        }
        {
            var Q0;
            {var subQ1=sQuery(id+"F7.wireOp",EDGE,"E76.MirrorCS");Q0=makeQuery(id+"F7.imprint","IMPRINT",FACE,{"disambiguationData":[TD([[makeQuery(id+"F7.imprint","IMPRINT",EDGE,{"derivedFrom":subQ1}),1.0]])]});}
            var Q1;
            {var subQ0=sQuery(id+"F7.wireOp",EDGE,"E68");Q1=makeQuery(id+"F7.imprint","IMPRINT",FACE,{"disambiguationData":[TD([[makeQuery(id+"F7.imprint","IMPRINT",EDGE,{"derivedFrom":subQ0}),-1.0]])]});}
            var Q2;
            {var subQ2=sQuery(id+"F7.wireOp",EDGE,"E72.MirrorCS");Q2=makeQuery(id+"F7.imprint","IMPRINT",FACE,{"disambiguationData":[TD([[makeQuery(id+"F7.imprint","IMPRINT",EDGE,{"derivedFrom":subQ2}),1.0]])]});}
            var Q3;
            {var subQ1=sQuery(id+"F7.wireOp",EDGE,"E78.MirrorCS");Q3=makeQuery(id+"F7.imprint","IMPRINT",FACE,{"disambiguationData":[TD([[makeQuery(id+"F7.imprint","IMPRINT",EDGE,{"derivedFrom":subQ1}),1.0]])]});}
            extrude(context, id + "F8", {"entities" : qUnion([Q0, Q1, Q2, Q3]), "operationType" : NewBodyOperationType.REMOVE, "endBound" : BoundingType.THROUGH_ALL, "oppositeDirection" : true, "depth" : 25.4 * mm});
        }
    });
